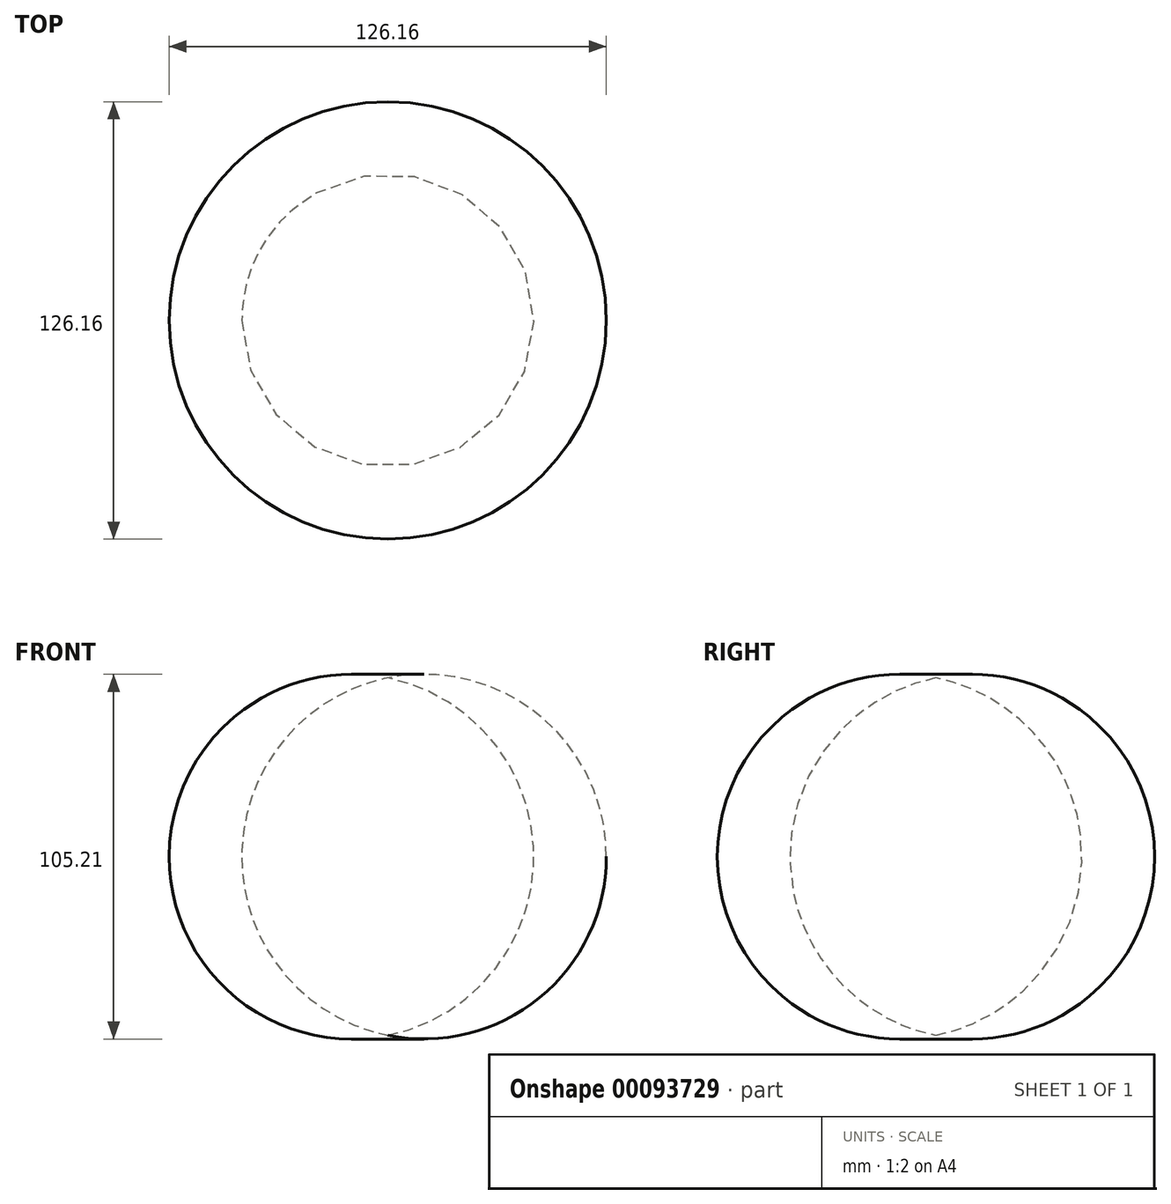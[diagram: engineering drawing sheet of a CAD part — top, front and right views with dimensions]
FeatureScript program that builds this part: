
annotation { "Feature Type Name" : "Feature", "Feature Type Description" : "" }
export const myFeature = defineFeature(function(context is Context, id is Id, definition is map)
    precondition{}
    {
        {
            var Q0;
            Q0=qCreatedBy(makeId("Front.planeOp"),FACE);
            var sketch = newSketch(context, id + "F0", { "sketchPlane" : qUnion([Q0])});
            skLineSegment(sketch, "E0", {"start": v(-46.19, 58.26) * mm, "end": v(-46.19, -44.85) * mm});
            skArc(sketch, "E1", {"start": v(-46.19, -44.85) * mm, "mid": v(-4.06, 6.7) * mm, "end": v(-46.19, 58.26) * mm});
            skSolve(sketch);
        }
        {
            var Q0;
            Q0=makeQuery(id+"F0.imprint","IMPRINT",FACE,{"disambiguationData":[TD([[makeQuery(id+"F0.imprint","IMPRINT",EDGE,{"derivedFrom":sQuery(id+"F0.wireOp",EDGE,"E0")}),1.0]])]});
            var Q1;
            Q1=sQuery(id+"F0.wireOp",EDGE,"E0");
            revolve(context, id + "F1", {"entities" : qUnion([Q0]), "axis" : qUnion([Q1]), "revolveType" : RevolveType.FULL});
        }
    });
